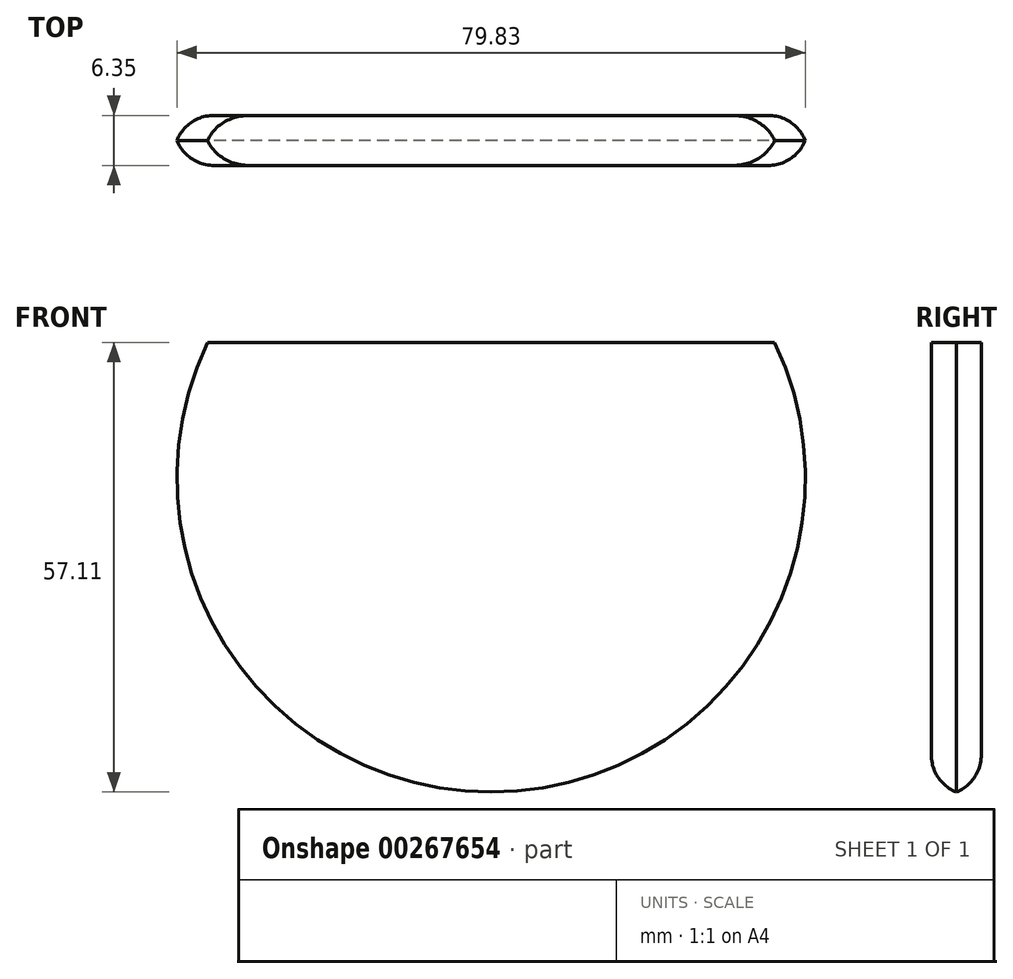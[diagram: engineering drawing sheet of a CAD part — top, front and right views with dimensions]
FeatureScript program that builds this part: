
annotation { "Feature Type Name" : "Feature", "Feature Type Description" : "" }
export const myFeature = defineFeature(function(context is Context, id is Id, definition is map)
    precondition{}
    {
        {
            var Q0;
            Q0=qCreatedBy(makeId("Front.planeOp"),FACE);
            var sketch = newSketch(context, id + "F0", { "sketchPlane" : qUnion([Q0])});
            skLineSegment(sketch, "E0", {"start": v(-36.63, 0) * mm, "end": v(36.23, 0) * mm});
            skArc(sketch, "E1", {"start": v(-36.63, 0) * mm, "mid": v(-0.2, -57.48) * mm, "end": v(36.23, 0) * mm});
            skSolve(sketch);
        }
        {
            var Q0;
            Q0=makeQuery(id+"F0.imprint","IMPRINT",FACE,{"disambiguationData":[TD([[makeQuery(id+"F0.imprint","IMPRINT",EDGE,{"derivedFrom":sQuery(id+"F0.wireOp",EDGE,"E0")}),-1.0]])]});
            extrude(context, id + "F1", {"entities" : qUnion([Q0]), "depth" : 6.35 * mm});
        }
        {
            var Q0;
            Q0=makeQuery(id+"F1.opExtrude","CAP_EDGE",EDGE,{"disambiguationData":[OSD([sQuery(id+"F0.wireOp",EDGE,"E1")])],"isStart":false});
            var Q1;
            Q1=makeQuery(id+"F1.opExtrude","CAP_EDGE",EDGE,{"disambiguationData":[OSD([sQuery(id+"F0.wireOp",EDGE,"E1")])],"isStart":true});
            fillet(context, id + "F2", {"entities" : qUnion([Q0, Q1]), "radius" : 5.08 * mm, "tangentPropagation" : true, "allowEdgeOverflow" : false});
        }
    });
